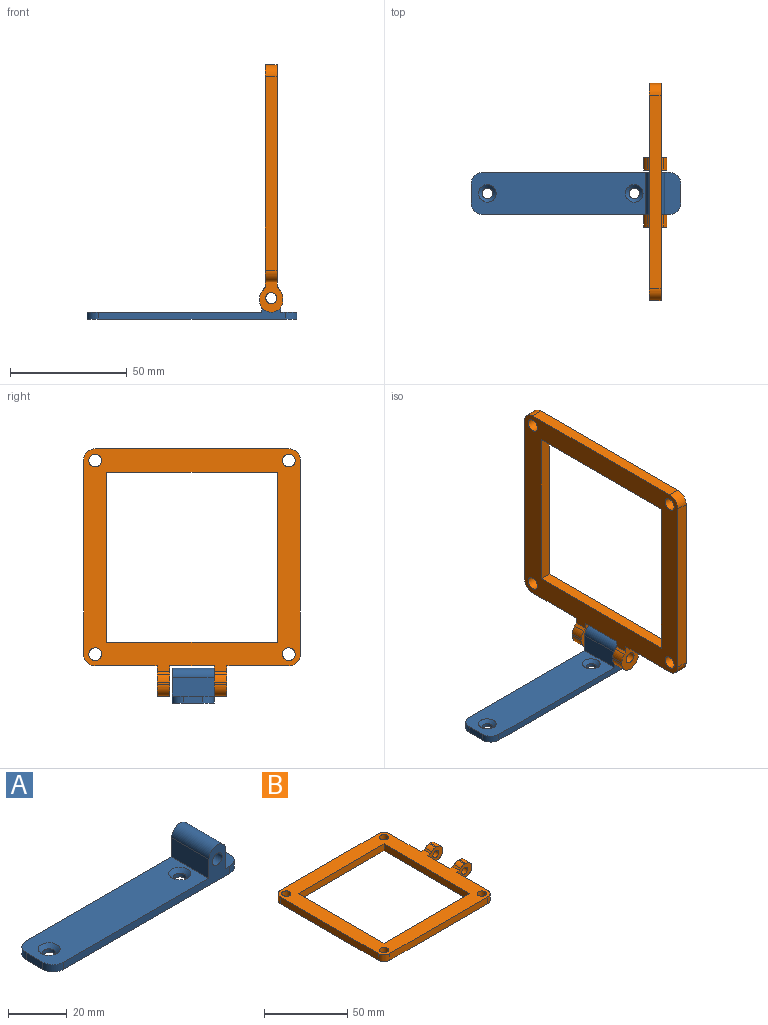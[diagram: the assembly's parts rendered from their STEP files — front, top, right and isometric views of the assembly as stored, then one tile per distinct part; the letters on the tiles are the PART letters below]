
ASSEMBLY  parts=2 mates=1
PART A: 19 faces, bbox 90x18x15 mm
  f0: plane 18x7mm, normal (0,0,1), area 115.3mm2, adj f1,f3,f6,f9,f17,f18
  f1: plane 80x15mm, normal (0,1,0), area 311mm2, adj f0,f7,f8,f9,f10,f11,f14,f15
  f2: plane 8x3mm, normal (-1,0,0), area 24mm2, adj f7,f8,f15,f16
  f3: plane 80x15mm, normal (0,-1,0), area 311mm2, adj f0,f7,f8,f9,f10,f11,f14,f16
  f4: cylinder r=2.25mm len=4.5mm, axis (0,0,-1), area 21.2mm2, adj f8,f13
  f5: cylinder r=2.25mm len=4.5mm, axis (0,0,-1), area 21.2mm2, adj f8,f12
  f6: plane 8x3mm, normal (1,0,0), area 24mm2, adj f0,f8,f17,f18
  f7: plane 75x18mm, normal (0,0,1), area 1250.9mm2, adj f1,f2,f3,f10,f12,f13,f15,f16
  f8: plane 90x18mm, normal (0,0,-1), area 1566.7mm2, adj f1,f2,f3,f4,f5,f6,f15,f16
  f9: plane 18x8mm, normal (1,0,0), area 144mm2, adj f0,f1,f3,f14
  f10: plane 18x8mm, normal (-1,0,0), area 144mm2, adj f1,f3,f7,f14
  f11: cylinder r=2.4mm len=18mm, axis (0,1,0), area 271.4mm2, adj f1,f3
  f12: cone r=2.25mm half-angle=45deg, axis (0,0,1), area 40mm2, adj f5,f7
  f13: cone r=2.25mm half-angle=45deg, axis (0,0,1), area 40mm2, adj f4,f7
  f14: cylinder r=4mm len=18mm, axis (0,-1,0), area 226.2mm2, adj f1,f3,f9,f10
  f15: cylinder r=5mm len=5mm, axis (0,0,1), area 23.6mm2, adj f1,f2,f7,f8
  f16: cylinder r=5mm len=5mm, axis (0,0,-1), area 23.6mm2, adj f2,f3,f7,f8
  f17: cylinder r=5mm len=5mm, axis (0,0,1), area 23.6mm2, adj f0,f3,f6,f8
  f18: cylinder r=5mm len=5mm, axis (0,0,-1), area 23.6mm2, adj f0,f1,f6,f8
PART B: 40 faces, bbox 106x93x10 mm
  f0: plane 26.5x5mm, normal (1,0,0), area 132.5mm2, adj f14,f15,f20,f38
  f1: plane 19x5mm, normal (1,0,0), area 95mm2, adj f14,f15,f16,f22
  f2: plane 83x5mm, normal (0,1,0), area 415mm2, adj f14,f15,f36,f39
  f3: plane 83x5mm, normal (-1,0,0), area 415mm2, adj f14,f15,f36,f37
  f4: plane 83x5mm, normal (0,-1,0), area 415mm2, adj f14,f15,f37,f38
  f5: plane 73x5mm, normal (1,0,0), area 365mm2, adj f6,f8,f14,f15
  f6: plane 73x5mm, normal (0,-1,0), area 365mm2, adj f5,f7,f14,f15
  f7: plane 73x5mm, normal (-1,0,0), area 365mm2, adj f6,f8,f14,f15
  f8: plane 73x5mm, normal (0,1,0), area 365mm2, adj f5,f7,f14,f15
  f9: cylinder r=2.75mm len=5.5mm, axis (0,0,-1), area 86.4mm2, adj f14,f15
  f10: cylinder r=2.75mm len=5.5mm, axis (0,0,-1), area 86.4mm2, adj f14,f15
  f11: cylinder r=2.75mm len=5.5mm, axis (0,0,-1), area 86.4mm2, adj f14,f15
  f12: cylinder r=2.75mm len=5.5mm, axis (0,0,-1), area 86.4mm2, adj f14,f15
  f13: plane 26.5x5mm, normal (1,0,0), area 132.5mm2, adj f14,f15,f18,f39
  f14: plane 95.5x93mm, normal (0,0,1), area 3231mm2, adj f0,f1,f2,f3,f4,f5,f6,f7
  f15: plane 95.5x93mm, normal (0,0,-1), area 3231mm2, adj f0,f1,f2,f3,f4,f5,f6,f7
  f16: plane 13x10mm, normal (0,-1,0), area 81.3mm2, adj f1,f14,f15,f17,f19,f25,f26,f28
  f17: plane 5.5x0.93mm, normal (0,0,-1), area 5.1mm2, adj f16,f18,f33,f34
  f18: plane 13x10mm, normal (0,1,0), area 81.3mm2, adj f13,f14,f15,f17,f19,f25,f26,f28
  f19: plane 5.5x0.93mm, normal (0,0,1), area 5.1mm2, adj f16,f18,f31,f34
  f20: plane 13x10mm, normal (0,-1,0), area 81.3mm2, adj f0,f14,f15,f21,f23,f24,f27,f29
  f21: plane 5.5x0.93mm, normal (0,0,-1), area 5.1mm2, adj f20,f22,f32,f35
  f22: plane 13x10mm, normal (0,1,0), area 81.3mm2, adj f1,f14,f15,f21,f23,f24,f27,f29
  f23: plane 5.5x0.93mm, normal (0,0,1), area 5.1mm2, adj f20,f22,f30,f35
  f24: cylinder r=2.4mm len=5.5mm, axis (0,1,0), area 82.9mm2, adj f20,f22
  f25: cylinder r=2.4mm len=5.5mm, axis (0,1,0), area 82.9mm2, adj f16,f18
  f26: plane 5.5x1.04mm, normal (-0.71,0,-0.71), area 8.1mm2, adj f15,f16,f18,f33
  f27: plane 5.5x1.04mm, normal (-0.71,0,-0.71), area 8.1mm2, adj f15,f20,f22,f32
  f28: plane 5.5x1.04mm, normal (-0.71,0,0.71), area 8.1mm2, adj f14,f16,f18,f31
  f29: plane 5.5x1.04mm, normal (-0.71,0,0.71), area 8.1mm2, adj f14,f20,f22,f30
  f30: cylinder r=5mm len=5.5mm, axis (0,-1,0), area 21.6mm2, adj f20,f22,f23,f29
  f31: cylinder r=5mm len=5.5mm, axis (0,-1,0), area 21.6mm2, adj f16,f18,f19,f28
  f32: cylinder r=5mm len=5.5mm, axis (0,1,0), area 21.6mm2, adj f20,f21,f22,f27
  f33: cylinder r=5mm len=5.5mm, axis (0,1,0), area 21.6mm2, adj f16,f17,f18,f26
  f34: cylinder r=5mm len=10mm, axis (0,-1,0), area 86.4mm2, adj f16,f17,f18,f19
  f35: cylinder r=5mm len=10mm, axis (0,1,0), area 86.4mm2, adj f20,f21,f22,f23
  f36: cylinder r=5mm len=5mm, axis (0,0,1), area 39.3mm2, adj f2,f3,f14,f15
  f37: cylinder r=5mm len=5mm, axis (0,0,-1), area 39.3mm2, adj f3,f4,f14,f15
  f38: cylinder r=5mm len=5mm, axis (0,0,1), area 39.3mm2, adj f0,f4,f14,f15
  f39: cylinder r=5mm len=5mm, axis (0,0,-1), area 39.3mm2, adj f2,f13,f14,f15
PLACE A t=(60.73,3.26,-29.22)mm
PLACE B rot(axis=(0,1,0),90deg) t=(95.55,-61.6,38.06)mm
MATE revolute B.f24 <-> A.f11  axis (0,1,0) through (98.05,-5.74,-20.22)mm
